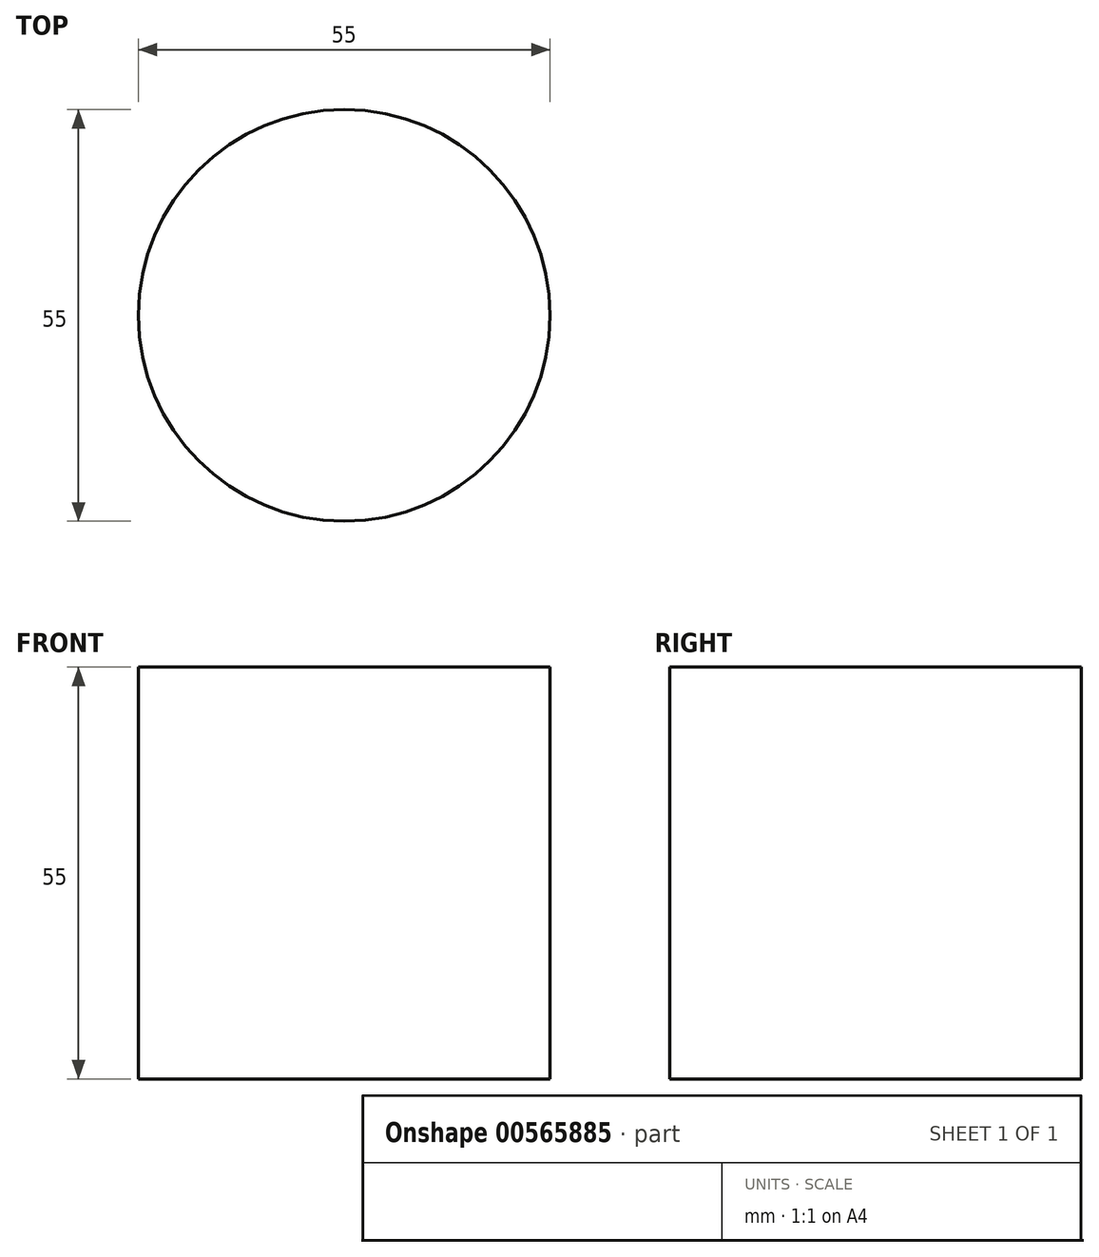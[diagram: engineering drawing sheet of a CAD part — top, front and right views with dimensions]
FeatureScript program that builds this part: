
annotation { "Feature Type Name" : "Feature", "Feature Type Description" : "" }
export const myFeature = defineFeature(function(context is Context, id is Id, definition is map)
    precondition{}
    {
        {
            var Q0;
            Q0=qCreatedBy(makeId("Top.planeOp"),FACE);
            var sketch = newSketch(context, id + "F0", { "sketchPlane" : qUnion([Q0])});
            skCircle(sketch, "E0", {"center": v(0, 0) * mm, "radius": 27.5 * mm});
            skSolve(sketch);
        }
        {
            var Q0;
            Q0 = qSketchRegion(id + "F0", true);
            extrude(context, id + "F1", {"entities" : qUnion([Q0]), "depth" : 55 * mm, "offsetDistance" : 25 * mm});
        }
    });
